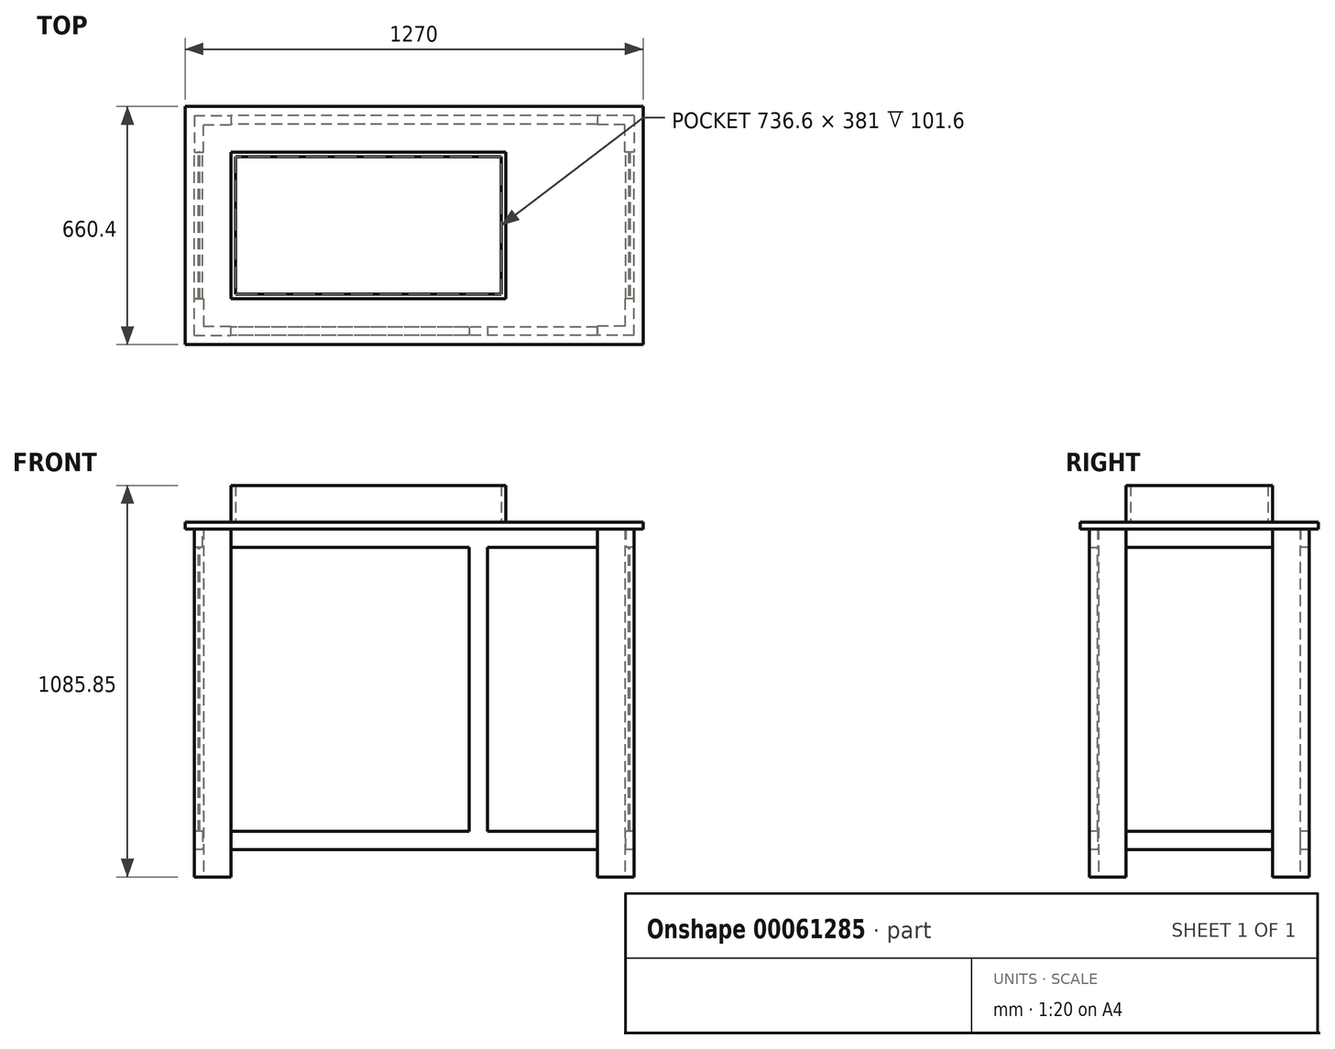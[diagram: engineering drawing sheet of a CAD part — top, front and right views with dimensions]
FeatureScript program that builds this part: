
annotation { "Feature Type Name" : "Feature", "Feature Type Description" : "" }
export const myFeature = defineFeature(function(context is Context, id is Id, definition is map)
    precondition{}
    {
        {
            var Q0;
            Q0=qCreatedBy(makeId("Top.planeOp"),FACE);
            var sketch = newSketch(context, id + "F0", { "sketchPlane" : qUnion([Q0])});
            skLineSegment(sketch, "E0.rect.bottom", {"start": v(609.6, 304.8) * mm, "end": v(-609.6, 304.8) * mm, "construction": true});
            skLineSegment(sketch, "E0.rect.top", {"start": v(609.6, -304.8) * mm, "end": v(-609.6, -304.8) * mm, "construction": true});
            skLineSegment(sketch, "E0.rect.left", {"start": v(609.6, 304.8) * mm, "end": v(609.6, -304.8) * mm, "construction": true});
            skLineSegment(sketch, "E0.rect.right", {"start": v(-609.6, 304.8) * mm, "end": v(-609.6, -304.8) * mm, "construction": true});
            skPoint(sketch, "E0.rect.middle", {"position": v(0, 0) * mm});
            skLineSegment(sketch, "E1.bottom", {"start": v(-609.6, 304.8) * mm, "end": v(-508, 304.8) * mm});
            skLineSegment(sketch, "E1.top", {"start": v(-584.2, 279.4) * mm, "end": v(-508, 279.4) * mm});
            skLineSegment(sketch, "E1.left", {"start": v(-609.6, 304.8) * mm, "end": v(-609.6, 203.2) * mm});
            skLineSegment(sketch, "E1.right", {"start": v(-508, 304.8) * mm, "end": v(-508, 279.4) * mm});
            skLineSegment(sketch, "E2", {"start": v(-609.6, 203.2) * mm, "end": v(-584.2, 203.2) * mm});
            skLineSegment(sketch, "E3", {"start": v(-584.2, 203.2) * mm, "end": v(-584.2, 279.4) * mm});
            skLineSegment(sketch, "E4.MirrorCS", {"start": v(508, 304.8) * mm, "end": v(508, 279.4) * mm});
            skLineSegment(sketch, "E5.MirrorCS", {"start": v(609.6, 203.2) * mm, "end": v(584.2, 203.2) * mm});
            skLineSegment(sketch, "E6.MirrorCS", {"start": v(609.6, 304.8) * mm, "end": v(508, 304.8) * mm});
            skLineSegment(sketch, "E7.MirrorCS", {"start": v(584.2, 203.2) * mm, "end": v(584.2, 279.4) * mm});
            skLineSegment(sketch, "E8.MirrorCS", {"start": v(609.6, 304.8) * mm, "end": v(609.6, 203.2) * mm});
            skLineSegment(sketch, "E9.MirrorCS", {"start": v(584.2, 279.4) * mm, "end": v(508, 279.4) * mm});
            skLineSegment(sketch, "E10.MirrorCS", {"start": v(-609.6, 304.8) * mm, "end": v(609.6, 304.8) * mm, "construction": true});
            skLineSegment(sketch, "E11.MirrorCS", {"start": v(508, -304.8) * mm, "end": v(508, -279.4) * mm});
            skLineSegment(sketch, "E12.MirrorCS", {"start": v(584.2, -279.4) * mm, "end": v(508, -279.4) * mm});
            skLineSegment(sketch, "E13.MirrorCS", {"start": v(584.2, -203.2) * mm, "end": v(584.2, -279.4) * mm});
            skLineSegment(sketch, "E14.MirrorCS", {"start": v(609.6, -203.2) * mm, "end": v(584.2, -203.2) * mm});
            skLineSegment(sketch, "E15.MirrorCS", {"start": v(609.6, -304.8) * mm, "end": v(609.6, -203.2) * mm});
            skLineSegment(sketch, "E16.MirrorCS", {"start": v(609.6, -304.8) * mm, "end": v(508, -304.8) * mm});
            skLineSegment(sketch, "E17.MirrorCS", {"start": v(-508, -304.8) * mm, "end": v(-508, -279.4) * mm});
            skLineSegment(sketch, "E18.MirrorCS", {"start": v(-584.2, -279.4) * mm, "end": v(-508, -279.4) * mm});
            skLineSegment(sketch, "E19.MirrorCS", {"start": v(-584.2, -203.2) * mm, "end": v(-584.2, -279.4) * mm});
            skLineSegment(sketch, "E20.MirrorCS", {"start": v(-609.6, -203.2) * mm, "end": v(-584.2, -203.2) * mm});
            skLineSegment(sketch, "E21.MirrorCS", {"start": v(-609.6, -304.8) * mm, "end": v(-508, -304.8) * mm});
            skLineSegment(sketch, "E22.MirrorCS", {"start": v(-609.6, -304.8) * mm, "end": v(-609.6, -203.2) * mm});
            skSolve(sketch);
        }
        {
            var Q0;
            Q0 = qSketchRegion(id + "F0", true);
            extrude(context, id + "F1", {"entities" : qUnion([Q0]), "depth" : 965.2 * mm});
        }
        {
            var Q0;
            Q0=makeQuery(id+"F1.opExtrude","SWEPT_FACE",FACE,{"disambiguationData":[OSD([sQuery(id+"F0.wireOp",EDGE,"E2")])]});
            var sketch = newSketch(context, id + "F2", { "sketchPlane" : qUnion([Q0])});
            skLineSegment(sketch, "E23.bottom", {"start": v(-609.6, 965.2) * mm, "end": v(-586.32, 965.2) * mm});
            skLineSegment(sketch, "E23.top", {"start": v(-609.6, 914.4) * mm, "end": v(-586.32, 914.4) * mm});
            skLineSegment(sketch, "E23.left", {"start": v(-609.6, 965.2) * mm, "end": v(-609.6, 914.4) * mm});
            skLineSegment(sketch, "E23.right", {"start": v(-586.32, 965.2) * mm, "end": v(-586.32, 914.4) * mm});
            skLineSegment(sketch, "E24.MirrorCS", {"start": v(586.32, 965.2) * mm, "end": v(586.32, 914.4) * mm});
            skLineSegment(sketch, "E25.MirrorCS", {"start": v(609.6, 965.2) * mm, "end": v(609.6, 914.4) * mm});
            skLineSegment(sketch, "E26.MirrorCS", {"start": v(609.6, 965.2) * mm, "end": v(586.32, 965.2) * mm});
            skLineSegment(sketch, "E27.MirrorCS", {"start": v(609.6, 914.4) * mm, "end": v(586.32, 914.4) * mm});
            skLineSegment(sketch, "E28.bottom", {"start": v(-609.6, 76.2) * mm, "end": v(-586.32, 76.2) * mm});
            skLineSegment(sketch, "E28.top", {"start": v(-609.6, 127) * mm, "end": v(-586.32, 127) * mm});
            skLineSegment(sketch, "E28.left", {"start": v(-609.6, 76.2) * mm, "end": v(-609.6, 127) * mm});
            skLineSegment(sketch, "E28.right", {"start": v(-586.32, 76.2) * mm, "end": v(-586.32, 127) * mm});
            skLineSegment(sketch, "E29.MirrorCS", {"start": v(609.6, 76.2) * mm, "end": v(586.32, 76.2) * mm});
            skLineSegment(sketch, "E30.MirrorCS", {"start": v(609.6, 127) * mm, "end": v(586.32, 127) * mm});
            skLineSegment(sketch, "E31.MirrorCS", {"start": v(586.32, 76.2) * mm, "end": v(586.32, 127) * mm});
            skLineSegment(sketch, "E32.MirrorCS", {"start": v(609.6, 76.2) * mm, "end": v(609.6, 127) * mm});
            skSolve(sketch);
        }
        {
            var Q0;
            Q0 = qSketchRegion(id + "F2", true);
            extrude(context, id + "F3", {"entities" : qUnion([Q0]), "endBound" : BoundingType.UP_TO_NEXT, "depth" : 25.4 * mm});
        }
        {
            var Q0;
            Q0=makeQuery(id+"F1.opExtrude","SWEPT_FACE",FACE,{"disambiguationData":[OSD([sQuery(id+"F0.wireOp",EDGE,"E1.right")])]});
            var sketch = newSketch(context, id + "F4", { "sketchPlane" : qUnion([Q0])});
            skLineSegment(sketch, "E33.bottom", {"start": v(304.8, 965.2) * mm, "end": v(281.52, 965.2) * mm});
            skLineSegment(sketch, "E33.top", {"start": v(304.8, 914.4) * mm, "end": v(281.52, 914.4) * mm});
            skLineSegment(sketch, "E33.left", {"start": v(304.8, 965.2) * mm, "end": v(304.8, 914.4) * mm});
            skLineSegment(sketch, "E33.right", {"start": v(281.52, 965.2) * mm, "end": v(281.52, 914.4) * mm});
            skLineSegment(sketch, "E34.bottom", {"start": v(304.8, 76.2) * mm, "end": v(281.52, 76.2) * mm});
            skLineSegment(sketch, "E34.top", {"start": v(304.8, 127) * mm, "end": v(281.52, 127) * mm});
            skLineSegment(sketch, "E34.left", {"start": v(304.8, 76.2) * mm, "end": v(304.8, 127) * mm});
            skLineSegment(sketch, "E34.right", {"start": v(281.52, 76.2) * mm, "end": v(281.52, 127) * mm});
            skLineSegment(sketch, "E35.MirrorCS", {"start": v(-281.52, 76.2) * mm, "end": v(-281.52, 127) * mm});
            skLineSegment(sketch, "E36.MirrorCS", {"start": v(-304.8, 76.2) * mm, "end": v(-304.8, 127) * mm});
            skLineSegment(sketch, "E37.MirrorCS", {"start": v(-304.8, 127) * mm, "end": v(-281.52, 127) * mm});
            skLineSegment(sketch, "E38.MirrorCS", {"start": v(-304.8, 76.2) * mm, "end": v(-281.52, 76.2) * mm});
            skLineSegment(sketch, "E39.MirrorCS", {"start": v(-281.52, 965.2) * mm, "end": v(-281.52, 914.4) * mm});
            skLineSegment(sketch, "E40.MirrorCS", {"start": v(-304.8, 965.2) * mm, "end": v(-304.8, 914.4) * mm});
            skLineSegment(sketch, "E41.MirrorCS", {"start": v(-304.8, 965.2) * mm, "end": v(-281.52, 965.2) * mm});
            skLineSegment(sketch, "E42.MirrorCS", {"start": v(-304.8, 914.4) * mm, "end": v(-281.52, 914.4) * mm});
            skSolve(sketch);
        }
        {
            var Q0;
            Q0 = qSketchRegion(id + "F4", true);
            extrude(context, id + "F5", {"entities" : qUnion([Q0]), "endBound" : BoundingType.UP_TO_NEXT, "depth" : 25.4 * mm});
        }
        {
            var Q0;
            Q0=makeQuery(id+"F1.opExtrude","CAP_FACE",FACE,{"disambiguationData":[OSD([sQuery(id+"F0.wireOp",EDGE,"E1.bottom"),sQuery(id+"F0.wireOp",EDGE,"E1.top"),sQuery(id+"F0.wireOp",EDGE,"E1.left"),sQuery(id+"F0.wireOp",EDGE,"E1.right"),sQuery(id+"F0.wireOp",EDGE,"E2"),sQuery(id+"F0.wireOp",EDGE,"E3")])],"isStart":false});
            var sketch = newSketch(context, id + "F6", { "sketchPlane" : qUnion([Q0])});
            skLineSegment(sketch, "E43.bottom", {"start": v(-635, 330.2) * mm, "end": v(635, 330.2) * mm});
            skLineSegment(sketch, "E43.top", {"start": v(-635, -330.2) * mm, "end": v(635, -330.2) * mm});
            skLineSegment(sketch, "E43.left", {"start": v(-635, 330.2) * mm, "end": v(-635, -330.2) * mm});
            skLineSegment(sketch, "E43.right", {"start": v(635, 330.2) * mm, "end": v(635, -330.2) * mm});
            skSolve(sketch);
        }
        {
            var Q0;
            Q0 = qSketchRegion(id + "F6", true);
            extrude(context, id + "F7", {"entities" : qUnion([Q0]), "depth" : 19.05 * mm});
        }
        {
            var Q0;
            Q0=makeQuery(id+"F3.opExtrude","SWEPT_FACE",FACE,{"disambiguationData":[OSD([sQuery(id+"F2.wireOp",EDGE,"E23.top")])]});
            var sketch = newSketch(context, id + "F8", { "sketchPlane" : qUnion([Q0])});
            skLineSegment(sketch, "E44.bottom", {"start": v(-597.96, -203.2) * mm, "end": v(-594.78, -203.2) * mm});
            skLineSegment(sketch, "E44.top", {"start": v(-597.96, 203.2) * mm, "end": v(-594.78, 203.2) * mm});
            skLineSegment(sketch, "E44.left", {"start": v(-597.96, -203.2) * mm, "end": v(-597.96, 203.2) * mm});
            skLineSegment(sketch, "E44.right", {"start": v(-594.78, -203.2) * mm, "end": v(-594.78, 203.2) * mm});
            skLineSegment(sketch, "E45.MirrorCS", {"start": v(597.96, 203.2) * mm, "end": v(594.78, 203.2) * mm});
            skLineSegment(sketch, "E46.MirrorCS", {"start": v(597.96, -203.2) * mm, "end": v(594.78, -203.2) * mm});
            skLineSegment(sketch, "E47.MirrorCS", {"start": v(594.78, -203.2) * mm, "end": v(594.78, 203.2) * mm});
            skLineSegment(sketch, "E48.MirrorCS", {"start": v(597.96, -203.2) * mm, "end": v(597.96, 203.2) * mm});
            skSolve(sketch);
        }
        {
            var Q0;
            Q0 = qSketchRegion(id + "F8", true);
            extrude(context, id + "F9", {"entities" : qUnion([Q0]), "endBound" : BoundingType.UP_TO_NEXT, "depth" : 25.4 * mm});
        }
        {
            var Q0;
            Q0=makeQuery(id+"F5.opExtrude","SWEPT_FACE",FACE,{"disambiguationData":[OSD([sQuery(id+"F4.wireOp",EDGE,"E42.MirrorCS")])]});
            var sketch = newSketch(context, id + "F10", { "sketchPlane" : qUnion([Q0])});
            skLineSegment(sketch, "E49.bottom", {"start": v(152.4, 304.8) * mm, "end": v(203.2, 304.8) * mm});
            skLineSegment(sketch, "E49.top", {"start": v(152.4, 281.52) * mm, "end": v(203.2, 281.52) * mm});
            skLineSegment(sketch, "E49.left", {"start": v(152.4, 304.8) * mm, "end": v(152.4, 281.52) * mm});
            skLineSegment(sketch, "E49.right", {"start": v(203.2, 304.8) * mm, "end": v(203.2, 281.52) * mm});
            skSolve(sketch);
        }
        {
            var Q0;
            Q0 = qSketchRegion(id + "F10", true);
            extrude(context, id + "F11", {"entities" : qUnion([Q0]), "operationType" : NewBodyOperationType.ADD, "endBound" : BoundingType.UP_TO_NEXT, "depth" : 25.4 * mm});
        }
        {
            var Q0;
            Q0=makeQuery(id+"F7.opExtrude","CAP_FACE",FACE,{"disambiguationData":[OSD([sQuery(id+"F6.wireOp",EDGE,"E43.bottom"),sQuery(id+"F6.wireOp",EDGE,"E43.top"),sQuery(id+"F6.wireOp",EDGE,"E43.left"),sQuery(id+"F6.wireOp",EDGE,"E43.right")])],"isStart":false});
            var sketch = newSketch(context, id + "F12", { "sketchPlane" : qUnion([Q0])});
            skLineSegment(sketch, "E50.bottom", {"start": v(-508, 203.2) * mm, "end": v(254, 203.2) * mm});
            skLineSegment(sketch, "E50.top", {"start": v(-508, -203.2) * mm, "end": v(254, -203.2) * mm});
            skLineSegment(sketch, "E50.left", {"start": v(-508, 203.2) * mm, "end": v(-508, -203.2) * mm});
            skLineSegment(sketch, "E50.right", {"start": v(254, 203.2) * mm, "end": v(254, -203.2) * mm});
            skLineSegment(sketch, "E51.0", {"start": v(241.3, 190.5) * mm, "end": v(241.3, -190.5) * mm});
            skLineSegment(sketch, "E51.1", {"start": v(-495.3, 190.5) * mm, "end": v(241.3, 190.5) * mm});
            skLineSegment(sketch, "E51.2", {"start": v(-495.3, 190.5) * mm, "end": v(-495.3, -190.5) * mm});
            skLineSegment(sketch, "E51.3", {"start": v(-495.3, -190.5) * mm, "end": v(241.3, -190.5) * mm});
            skSolve(sketch);
        }
        {
            var Q0;
            Q0 = qSketchRegion(id + "F12", true);
            extrude(context, id + "F13", {"entities" : qUnion([Q0]), "operationType" : NewBodyOperationType.ADD, "depth" : 101.6 * mm});
        }
    });
